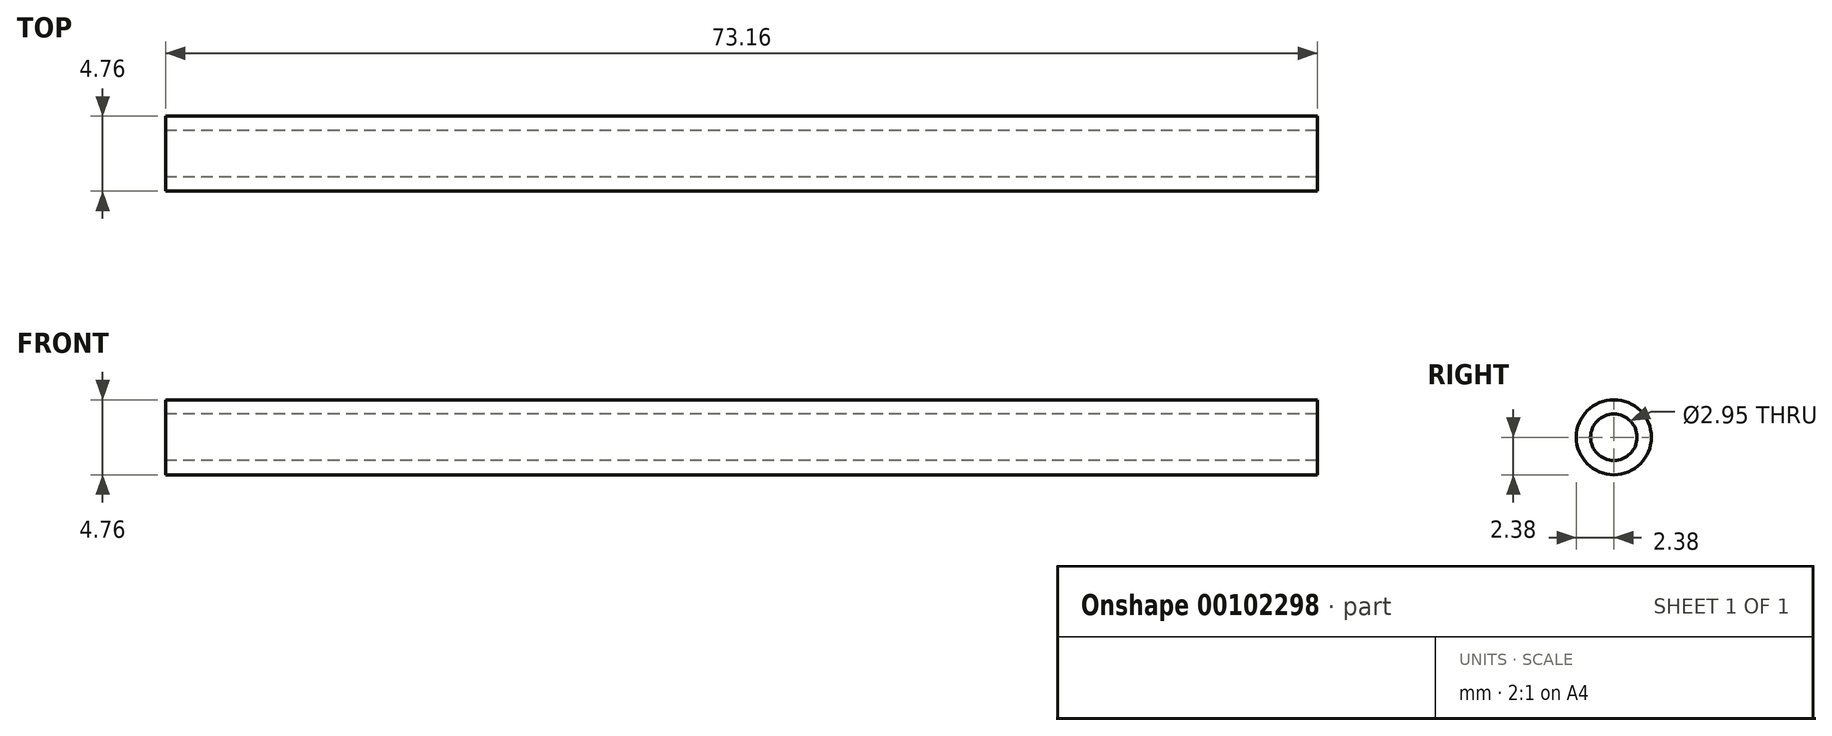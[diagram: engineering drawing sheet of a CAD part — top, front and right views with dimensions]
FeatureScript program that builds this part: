
annotation { "Feature Type Name" : "Feature", "Feature Type Description" : "" }
export const myFeature = defineFeature(function(context is Context, id is Id, definition is map)
    precondition{}
    {
        {
            var Q0;
            Q0=qCreatedBy(makeId("Right.planeOp"),FACE);
            var sketch = newSketch(context, id + "F0", { "sketchPlane" : qUnion([Q0])});
            skCircle(sketch, "E0", {"center": v(0, 0) * mm, "radius": 2.38 * mm});
            skCircle(sketch, "E1", {"center": v(0, 0) * mm, "radius": 1.47 * mm});
            skSolve(sketch);
        }
        {
            var Q0;
            Q0=qSketchRegion(id+"F0",true);
            extrude(context, id + "F1", {"entities" : qUnion([Q0]), "endBound" : BoundingType.SYMMETRIC, "depth" : 73.15 * mm});
        }
    });
